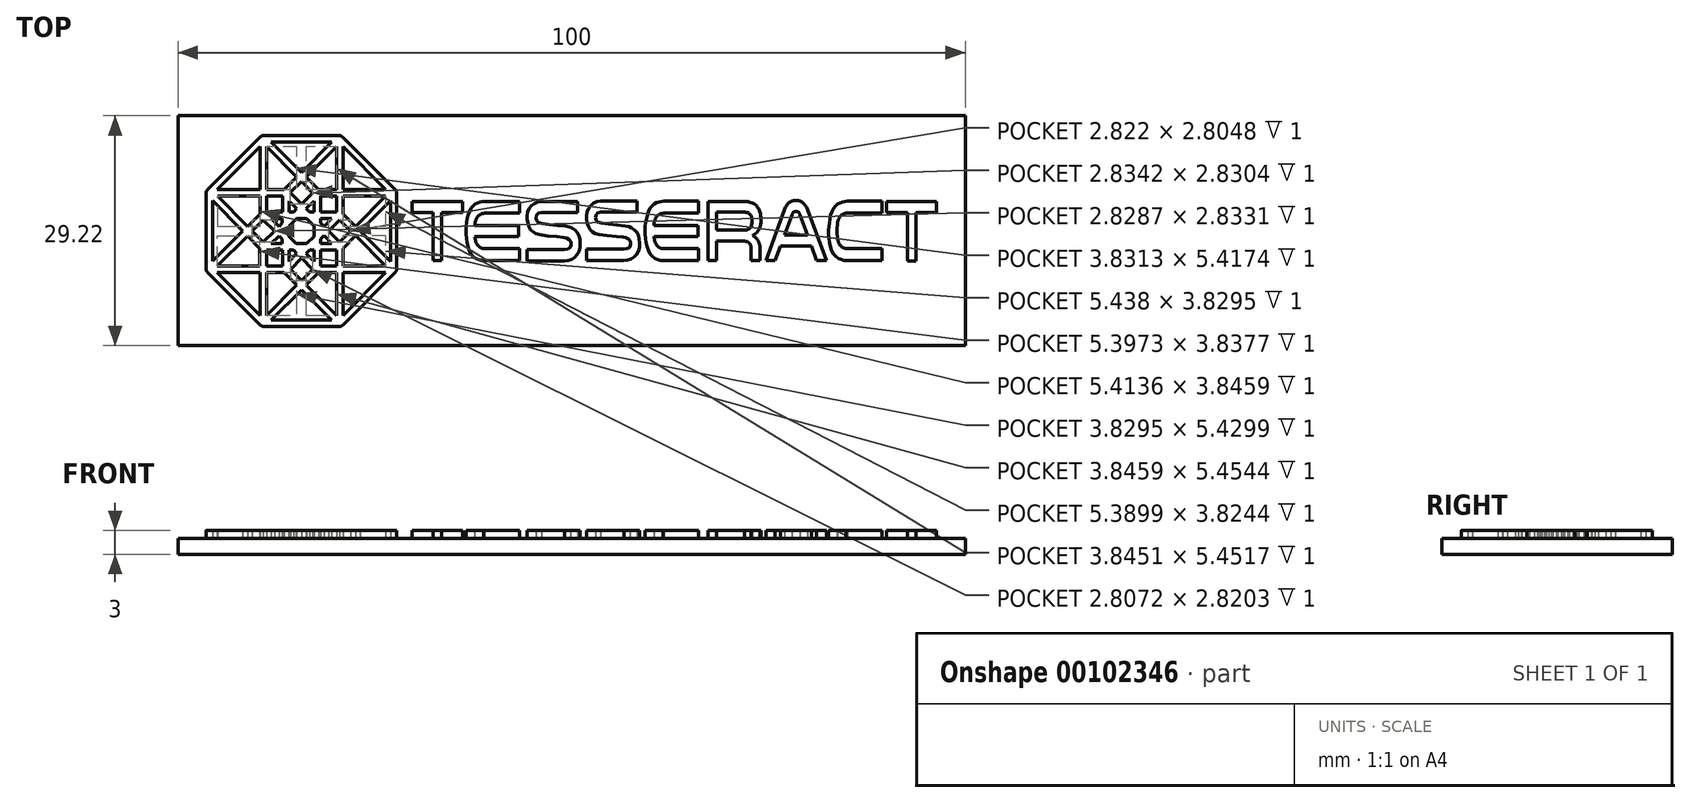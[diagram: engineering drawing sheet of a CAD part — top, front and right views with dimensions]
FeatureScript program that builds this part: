
annotation { "Feature Type Name" : "Feature", "Feature Type Description" : "" }
export const myFeature = defineFeature(function(context is Context, id is Id, definition is map)
    precondition{}
    {
        {
            var Q0;
            Q0=qCreatedBy(makeId("Top.planeOp"),FACE);
            var sketch = newSketch(context, id + "F0", { "sketchPlane" : qUnion([Q0])});
            skLineSegment(sketch, "E0.bottom", {"start": v(-42.05, 26.1) * mm, "end": v(57.95, 26.1) * mm});
            skLineSegment(sketch, "E0.top", {"start": v(-42.05, -3.12) * mm, "end": v(57.95, -3.12) * mm});
            skLineSegment(sketch, "E0.left", {"start": v(-42.05, 26.1) * mm, "end": v(-42.05, -3.12) * mm});
            skLineSegment(sketch, "E0.right", {"start": v(57.95, 26.1) * mm, "end": v(57.95, -3.12) * mm});
            skSolve(sketch);
        }
        {
            var Q0;
            Q0=makeQuery(id+"F0.imprint","IMPRINT",FACE,{"disambiguationData":[TD([[makeQuery(id+"F0.imprint","IMPRINT",EDGE,{"derivedFrom":sQuery(id+"F0.wireOp",EDGE,"E0.bottom")}),-1.0]])]});
            extrude(context, id + "F1", {"entities" : qUnion([Q0]), "oppositeDirection" : true, "depth" : 2 * mm});
        }
        {
            var Q0;
            Q0=makeQuery(id+"F1.opExtrude","CAP_FACE",FACE,{"disambiguationData":[OSD([sQuery(id+"F0.wireOp",EDGE,"E0.bottom"),sQuery(id+"F0.wireOp",EDGE,"E0.top"),sQuery(id+"F0.wireOp",EDGE,"E0.left"),sQuery(id+"F0.wireOp",EDGE,"E0.right")])],"isStart":true});
            var sketch = newSketch(context, id + "F2", { "sketchPlane" : qUnion([Q0])});
            skLineSegment(sketch, "E1.bottom", {"start": v(-12.32, 15.2) * mm, "end": v(-5.94, 15.2) * mm});
            skLineSegment(sketch, "E1.top", {"start": v(-12.32, 13.79) * mm, "end": v(-9.67, 13.79) * mm});
            skLineSegment(sketch, "E1.left", {"start": v(-12.32, 15.2) * mm, "end": v(-12.32, 13.79) * mm});
            skLineSegment(sketch, "E1.right", {"start": v(-5.94, 15.2) * mm, "end": v(-5.94, 13.79) * mm});
            skLineSegment(sketch, "E2.bottom", {"start": v(-9.67, 7.67) * mm, "end": v(-8.58, 7.67) * mm});
            skLineSegment(sketch, "E2.left", {"start": v(-9.67, 7.67) * mm, "end": v(-9.67, 13.79) * mm});
            skLineSegment(sketch, "E2.right", {"start": v(-8.58, 7.67) * mm, "end": v(-8.58, 13.79) * mm});
            skLineSegment(sketch, "E3.trimOffspring", {"start": v(-8.58, 13.79) * mm, "end": v(-5.94, 13.79) * mm});
            skLineSegment(sketch, "E4.bottom", {"start": v(1.34, 13.7) * mm, "end": v(-3.1, 13.7) * mm});
            skLineSegment(sketch, "E4.top", {"start": v(1.34, 15.22) * mm, "end": v(-3.1, 15.22) * mm});
            skLineSegment(sketch, "E4.left", {"start": v(1.34, 13.7) * mm, "end": v(1.34, 15.22) * mm});
            skLineSegment(sketch, "E5.bottom", {"start": v(1.23, 12.16) * mm, "end": v(-4.36, 12.16) * mm});
            skLineSegment(sketch, "E5.top", {"start": v(1.23, 10.75) * mm, "end": v(-4.36, 10.75) * mm});
            skLineSegment(sketch, "E5.left", {"start": v(1.23, 12.16) * mm, "end": v(1.23, 10.75) * mm});
            skLineSegment(sketch, "E6.bottom", {"start": v(1.32, 9.22) * mm, "end": v(-3.23, 9.22) * mm});
            skLineSegment(sketch, "E6.top", {"start": v(1.32, 7.67) * mm, "end": v(-3.23, 7.67) * mm});
            skLineSegment(sketch, "E6.left", {"start": v(1.32, 9.22) * mm, "end": v(1.32, 7.67) * mm});
            skFitSpline(sketch, "E7", {"points": [v(-3.23, 9.22) * mm, v(-3.64, 9.32) * mm, v(-4.1, 9.77) * mm, v(-4.36, 10.75) * mm, v(-4.36, 12.16) * mm, v(-4.2, 12.95) * mm, v(-3.83, 13.45) * mm, v(-3.1, 13.7) * mm], "startDerivative": vector(-3.91, 0.56) * mm, "endDerivative": vector(8.28, 0.62) * mm});
            skFitSpline(sketch, "E8", {"points": [v(-3.23, 7.67) * mm, v(-3.9, 7.8) * mm, v(-4.7, 8.36) * mm, v(-5.31, 9.73) * mm, v(-5.48, 11.49) * mm, v(-5.35, 12.85) * mm, v(-4.89, 14.25) * mm, v(-4.33, 14.85) * mm, v(-3.68, 15.16) * mm, v(-3.1, 15.22) * mm], "startDerivative": vector(-7.35, 0.76) * mm, "endDerivative": vector(6.93, 0.14) * mm});
            skLineSegment(sketch, "E9.bottom", {"start": v(8.7, 13.79) * mm, "end": v(4.1, 13.79) * mm});
            skLineSegment(sketch, "E9.top", {"start": v(8.7, 15.22) * mm, "end": v(4.1, 15.22) * mm});
            skLineSegment(sketch, "E9.left", {"start": v(8.7, 13.79) * mm, "end": v(8.7, 15.22) * mm});
            skLineSegment(sketch, "E10.bottom", {"start": v(2.27, 7.65) * mm, "end": v(7.07, 7.65) * mm});
            skLineSegment(sketch, "E10.top", {"start": v(2.27, 9.08) * mm, "end": v(7.07, 9.08) * mm});
            skLineSegment(sketch, "E10.left", {"start": v(2.27, 7.65) * mm, "end": v(2.27, 9.08) * mm});
            skFitSpline(sketch, "E11", {"points": [v(7.07, 9.08) * mm, v(7.53, 9.18) * mm, v(7.81, 9.41) * mm, v(7.87, 9.86) * mm, v(7.75, 10.29) * mm, v(7.27, 10.57) * mm, v(6.93, 10.63) * mm, v(3.75, 11) * mm, v(3.25, 11.18) * mm, v(2.8, 11.54) * mm, v(2.49, 12.03) * mm, v(2.32, 12.78) * mm, v(2.3, 13.41) * mm, v(2.47, 14.12) * mm, v(2.86, 14.68) * mm, v(3.43, 15.05) * mm, v(4.1, 15.22) * mm], "startDerivative": vector(9.28, 1.26) * mm, "endDerivative": vector(10.61, 2.02) * mm});
            skFitSpline(sketch, "E12", {"points": [v(7.07, 7.65) * mm, v(7.67, 7.76) * mm, v(8.33, 8.09) * mm, v(8.79, 8.66) * mm, v(9, 9.43) * mm, v(8.98, 10.38) * mm, v(8.85, 10.93) * mm, v(8.44, 11.5) * mm, v(7.9, 11.87) * mm, v(7.39, 12.03) * mm, v(4.2, 12.4) * mm, v(3.62, 12.63) * mm, v(3.45, 12.93) * mm, v(3.44, 13.32) * mm, v(3.63, 13.65) * mm, v(4.1, 13.79) * mm], "startDerivative": vector(9.62, 1.1) * mm, "endDerivative": vector(9.31, 1.4) * mm});
            skLineSegment(sketch, "E13.bottom", {"start": v(16.24, 13.83) * mm, "end": v(11.64, 13.83) * mm});
            skLineSegment(sketch, "E13.top", {"start": v(16.24, 15.26) * mm, "end": v(11.64, 15.26) * mm});
            skLineSegment(sketch, "E13.left", {"start": v(16.24, 13.83) * mm, "end": v(16.24, 15.26) * mm});
            skLineSegment(sketch, "E14.bottom", {"start": v(9.82, 7.7) * mm, "end": v(14.62, 7.7) * mm});
            skLineSegment(sketch, "E14.top", {"start": v(9.82, 9.13) * mm, "end": v(14.62, 9.13) * mm});
            skLineSegment(sketch, "E14.left", {"start": v(9.82, 7.7) * mm, "end": v(9.82, 9.13) * mm});
            skFitSpline(sketch, "E15", {"points": [v(14.62, 9.13) * mm, v(15.08, 9.23) * mm, v(15.36, 9.46) * mm, v(15.43, 9.9) * mm, v(15.3, 10.33) * mm, v(14.82, 10.61) * mm, v(14.48, 10.68) * mm, v(11.3, 11.04) * mm, v(10.8, 11.22) * mm, v(10.34, 11.58) * mm, v(10.04, 12.07) * mm, v(9.87, 12.83) * mm, v(9.85, 13.46) * mm, v(10.02, 14.17) * mm, v(10.4, 14.72) * mm, v(10.98, 15.1) * mm, v(11.64, 15.26) * mm], "startDerivative": vector(9.28, 1.26) * mm, "endDerivative": vector(10.61, 2.02) * mm});
            skFitSpline(sketch, "E16", {"points": [v(14.62, 7.7) * mm, v(15.22, 7.8) * mm, v(15.88, 8.14) * mm, v(16.34, 8.7) * mm, v(16.55, 9.48) * mm, v(16.53, 10.43) * mm, v(16.4, 10.97) * mm, v(15.99, 11.54) * mm, v(15.45, 11.91) * mm, v(14.94, 12.07) * mm, v(11.75, 12.45) * mm, v(11.17, 12.67) * mm, v(11, 12.98) * mm, v(11, 13.37) * mm, v(11.18, 13.7) * mm, v(11.64, 13.83) * mm], "startDerivative": vector(9.62, 1.1) * mm, "endDerivative": vector(9.31, 1.4) * mm});
            skLineSegment(sketch, "E17.bottom", {"start": v(24.09, 13.7) * mm, "end": v(19.65, 13.7) * mm});
            skLineSegment(sketch, "E17.top", {"start": v(24.09, 15.22) * mm, "end": v(19.65, 15.22) * mm});
            skLineSegment(sketch, "E17.left", {"start": v(24.09, 13.7) * mm, "end": v(24.09, 15.22) * mm});
            skLineSegment(sketch, "E18.bottom", {"start": v(23.98, 12.17) * mm, "end": v(18.4, 12.17) * mm});
            skLineSegment(sketch, "E18.top", {"start": v(23.98, 10.76) * mm, "end": v(18.4, 10.76) * mm});
            skLineSegment(sketch, "E18.left", {"start": v(23.98, 12.17) * mm, "end": v(23.98, 10.76) * mm});
            skLineSegment(sketch, "E19.bottom", {"start": v(24.07, 9.2) * mm, "end": v(19.53, 9.2) * mm});
            skLineSegment(sketch, "E19.top", {"start": v(24.07, 7.68) * mm, "end": v(19.53, 7.68) * mm});
            skLineSegment(sketch, "E19.left", {"start": v(24.07, 9.2) * mm, "end": v(24.07, 7.68) * mm});
            skFitSpline(sketch, "E20", {"points": [v(19.53, 9.2) * mm, v(19.12, 9.33) * mm, v(18.66, 9.78) * mm, v(18.4, 10.76) * mm, v(18.4, 12.17) * mm, v(18.56, 12.95) * mm, v(18.92, 13.45) * mm, v(19.65, 13.7) * mm], "startDerivative": vector(-3.91, 0.56) * mm, "endDerivative": vector(8.28, 0.62) * mm});
            skFitSpline(sketch, "E21", {"points": [v(19.53, 7.68) * mm, v(18.86, 7.8) * mm, v(18.05, 8.37) * mm, v(17.44, 9.73) * mm, v(17.28, 11.5) * mm, v(17.4, 12.85) * mm, v(17.86, 14.25) * mm, v(18.42, 14.85) * mm, v(19.08, 15.16) * mm, v(19.65, 15.22) * mm], "startDerivative": vector(-7.35, 0.76) * mm, "endDerivative": vector(6.93, 0.14) * mm});
            skLineSegment(sketch, "E22.bottom", {"start": v(47.93, 15.2) * mm, "end": v(54.31, 15.2) * mm});
            skLineSegment(sketch, "E22.top", {"start": v(47.93, 13.78) * mm, "end": v(50.58, 13.78) * mm});
            skLineSegment(sketch, "E22.left", {"start": v(47.93, 15.2) * mm, "end": v(47.93, 13.78) * mm});
            skLineSegment(sketch, "E22.right", {"start": v(54.31, 15.2) * mm, "end": v(54.31, 13.78) * mm});
            skLineSegment(sketch, "E23.bottom", {"start": v(50.58, 7.66) * mm, "end": v(51.67, 7.66) * mm});
            skLineSegment(sketch, "E23.left", {"start": v(50.58, 7.66) * mm, "end": v(50.58, 13.78) * mm});
            skLineSegment(sketch, "E23.right", {"start": v(51.67, 7.66) * mm, "end": v(51.67, 13.78) * mm});
            skLineSegment(sketch, "E24.trimOffspring", {"start": v(51.67, 13.78) * mm, "end": v(54.31, 13.78) * mm});
            skLineSegment(sketch, "E25.bottom", {"start": v(25.25, 7.67) * mm, "end": v(26.37, 7.67) * mm});
            skLineSegment(sketch, "E25.top", {"start": v(25.25, 15.22) * mm, "end": v(26.37, 15.22) * mm});
            skLineSegment(sketch, "E25.left", {"start": v(25.25, 7.67) * mm, "end": v(25.25, 15.22) * mm});
            skLineSegment(sketch, "E25.right", {"start": v(26.37, 7.67) * mm, "end": v(26.37, 10.15) * mm});
            skLineSegment(sketch, "E26.bottom", {"start": v(26.37, 11.57) * mm, "end": v(29.9, 11.57) * mm});
            skLineSegment(sketch, "E26.top", {"start": v(26.37, 10.15) * mm, "end": v(29.9, 10.15) * mm});
            skLineSegment(sketch, "E27.bottom", {"start": v(26.37, 15.22) * mm, "end": v(29.95, 15.22) * mm});
            skLineSegment(sketch, "E27.top", {"start": v(26.37, 13.83) * mm, "end": v(29.95, 13.83) * mm});
            skLineSegment(sketch, "E28.trimOffspring", {"start": v(26.37, 11.57) * mm, "end": v(26.37, 13.83) * mm});
            skFitSpline(sketch, "E29", {"points": [v(29.95, 13.83) * mm, v(30.39, 13.74) * mm, v(30.69, 13.42) * mm, v(30.87, 12.72) * mm, v(30.71, 12) * mm, v(30.37, 11.65) * mm, v(29.9, 11.57) * mm], "startDerivative": vector(3.1, -0.3) * mm, "endDerivative": vector(-3.16, -0.18) * mm});
            skFitSpline(sketch, "E30", {"points": [v(30.93, 10.88) * mm, v(31.31, 11.1) * mm, v(31.7, 11.56) * mm, v(31.94, 12.2) * mm, v(32, 12.98) * mm, v(31.9, 13.75) * mm, v(31.62, 14.38) * mm, v(31.1, 14.9) * mm, v(30.56, 15.13) * mm, v(30.3, 15.2) * mm, v(29.95, 15.22) * mm], "startDerivative": vector(4.45, 2.16) * mm, "endDerivative": vector(-4.85, 0.22) * mm});
            skLineSegment(sketch, "E31.bottom", {"start": v(30.73, 7.68) * mm, "end": v(31.87, 7.68) * mm});
            skLineSegment(sketch, "E31.left", {"start": v(30.73, 7.68) * mm, "end": v(30.73, 9.36) * mm});
            skLineSegment(sketch, "E31.right", {"start": v(31.87, 7.68) * mm, "end": v(31.87, 9.36) * mm});
            skFitSpline(sketch, "E32", {"points": [v(29.9, 10.15) * mm, v(30.22, 10.1) * mm, v(30.45, 9.96) * mm, v(30.63, 9.74) * mm, v(30.7, 9.55) * mm, v(30.73, 9.36) * mm], "startDerivative": vector(1.5, -0.05) * mm, "endDerivative": vector(0.26, -0.85) * mm});
            skFitSpline(sketch, "E33", {"points": [v(30.93, 10.88) * mm, v(31.14, 10.77) * mm, v(31.37, 10.57) * mm, v(31.63, 10.22) * mm, v(31.77, 9.87) * mm, v(31.84, 9.64) * mm, v(31.87, 9.47) * mm, v(31.87, 9.36) * mm], "startDerivative": vector(1.44, -0.68) * mm, "endDerivative": vector(0.02, -1.5) * mm});
            skLineSegment(sketch, "E34", {"start": v(32.62, 7.67) * mm, "end": v(33.8, 7.67) * mm});
            skLineSegment(sketch, "E35", {"start": v(33.8, 7.67) * mm, "end": v(34.48, 9.55) * mm});
            skLineSegment(sketch, "E36", {"start": v(34.48, 9.55) * mm, "end": v(38.4, 9.55) * mm});
            skLineSegment(sketch, "E37", {"start": v(38.4, 9.55) * mm, "end": v(39.06, 7.67) * mm});
            skLineSegment(sketch, "E38", {"start": v(39.06, 7.67) * mm, "end": v(40.3, 7.67) * mm});
            skLineSegment(sketch, "E39", {"start": v(40.3, 7.67) * mm, "end": v(37.91, 14.2) * mm});
            skLineSegment(sketch, "E40", {"start": v(34.97, 14.2) * mm, "end": v(32.62, 7.67) * mm});
            skLineSegment(sketch, "E41", {"start": v(34.98, 10.95) * mm, "end": v(37.88, 10.95) * mm});
            skLineSegment(sketch, "E42", {"start": v(37.88, 10.95) * mm, "end": v(36.95, 13.5) * mm});
            skLineSegment(sketch, "E43", {"start": v(35.9, 13.5) * mm, "end": v(34.98, 10.95) * mm});
            skFitSpline(sketch, "E44", {"points": [v(35.9, 13.5) * mm, v(36.06, 13.77) * mm, v(36.26, 13.91) * mm, v(36.43, 13.94) * mm, v(36.66, 13.9) * mm, v(36.84, 13.7) * mm, v(36.95, 13.5) * mm], "startDerivative": vector(0.68, 1.52) * mm, "endDerivative": vector(0.61, -1.19) * mm});
            skFitSpline(sketch, "E45", {"points": [v(34.97, 14.2) * mm, v(35.24, 14.68) * mm, v(35.63, 15.1) * mm, v(35.99, 15.27) * mm, v(36.83, 15.28) * mm, v(37.3, 15.06) * mm, v(37.66, 14.65) * mm, v(37.91, 14.2) * mm], "startDerivative": vector(1.68, 3.45) * mm, "endDerivative": vector(1.65, -3.33) * mm});
            skLineSegment(sketch, "E46.bottom", {"start": v(47.38, 13.72) * mm, "end": v(42.95, 13.72) * mm});
            skLineSegment(sketch, "E46.top", {"start": v(47.38, 15.23) * mm, "end": v(42.97, 15.23) * mm});
            skLineSegment(sketch, "E46.left", {"start": v(47.38, 13.72) * mm, "end": v(47.38, 15.23) * mm});
            skLineSegment(sketch, "E47.bottom", {"start": v(47.36, 9.21) * mm, "end": v(42.82, 9.21) * mm});
            skLineSegment(sketch, "E47.top", {"start": v(47.36, 7.68) * mm, "end": v(42.81, 7.68) * mm});
            skLineSegment(sketch, "E47.left", {"start": v(47.36, 9.21) * mm, "end": v(47.36, 7.68) * mm});
            skFitSpline(sketch, "E48", {"points": [v(42.82, 9.21) * mm, v(42.41, 9.34) * mm, v(41.95, 9.79) * mm, v(41.69, 10.77) * mm, v(41.69, 12.18) * mm, v(41.85, 12.96) * mm, v(42.22, 13.46) * mm, v(42.95, 13.72) * mm], "startDerivative": vector(-3.91, 0.56) * mm, "endDerivative": vector(8.28, 0.62) * mm});
            skFitSpline(sketch, "E49", {"points": [v(42.81, 7.68) * mm, v(42.21, 7.8) * mm, v(41.36, 8.3) * mm, v(40.75, 9.67) * mm, v(40.59, 11.43) * mm, v(40.71, 12.79) * mm, v(41.13, 14.2) * mm, v(41.72, 14.84) * mm, v(42.35, 15.13) * mm, v(42.97, 15.23) * mm], "startDerivative": vector(-7.35, 0.76) * mm, "endDerivative": vector(6.93, 0.14) * mm});
            skFitSpline(sketch, "E50", {"points": [v(41.69, 10.77) * mm, v(41.67, 11.4) * mm, v(41.69, 12.18) * mm], "startDerivative": vector(-0.09, 1.41) * mm, "endDerivative": vector(0.09, 1.4) * mm});
            skLineSegment(sketch, "E51", {"start": v(-27.98, 10.78) * mm, "end": v(-27.04, 9.85) * mm});
            skLineSegment(sketch, "E52", {"start": v(-27.04, 9.85) * mm, "end": v(-25.74, 9.85) * mm});
            skLineSegment(sketch, "E53", {"start": v(-25.74, 9.85) * mm, "end": v(-24.79, 10.77) * mm});
            skLineSegment(sketch, "E54", {"start": v(-24.79, 10.77) * mm, "end": v(-24.79, 12.1) * mm});
            skLineSegment(sketch, "E55", {"start": v(-24.79, 12.1) * mm, "end": v(-25.7, 13.04) * mm});
            skLineSegment(sketch, "E56", {"start": v(-25.7, 13.04) * mm, "end": v(-27.01, 13.04) * mm});
            skLineSegment(sketch, "E57", {"start": v(-27.01, 13.04) * mm, "end": v(-27.97, 12.1) * mm});
            skLineSegment(sketch, "E58", {"start": v(-27.97, 12.1) * mm, "end": v(-27.98, 10.78) * mm});
            skLineSegment(sketch, "E59", {"start": v(-23.95, 12.44) * mm, "end": v(-23.95, 13.04) * mm});
            skLineSegment(sketch, "E60", {"start": v(-23.95, 13.04) * mm, "end": v(-22.55, 13.04) * mm});
            skLineSegment(sketch, "E61", {"start": v(-22.55, 13.04) * mm, "end": v(-23.53, 12.03) * mm});
            skLineSegment(sketch, "E62", {"start": v(-23.53, 12.03) * mm, "end": v(-23.95, 12.44) * mm});
            skLineSegment(sketch, "E63", {"start": v(-23.96, 10.44) * mm, "end": v(-23.96, 9.84) * mm});
            skLineSegment(sketch, "E64", {"start": v(-23.96, 9.84) * mm, "end": v(-22.55, 9.84) * mm});
            skLineSegment(sketch, "E65", {"start": v(-22.55, 9.84) * mm, "end": v(-23.53, 10.85) * mm});
            skLineSegment(sketch, "E66", {"start": v(-23.53, 10.85) * mm, "end": v(-23.96, 10.44) * mm});
            skLineSegment(sketch, "E67", {"start": v(-22.94, 11.46) * mm, "end": v(-21.52, 10.03) * mm});
            skLineSegment(sketch, "E68", {"start": v(-21.52, 10.03) * mm, "end": v(-20.12, 11.42) * mm});
            skLineSegment(sketch, "E69", {"start": v(-20.12, 11.42) * mm, "end": v(-21.52, 12.83) * mm});
            skLineSegment(sketch, "E70", {"start": v(-21.52, 12.83) * mm, "end": v(-22.94, 11.46) * mm});
            skLineSegment(sketch, "E71", {"start": v(-27.97, 13.86) * mm, "end": v(-27.38, 13.86) * mm});
            skLineSegment(sketch, "E72", {"start": v(-27.38, 13.86) * mm, "end": v(-26.97, 14.28) * mm});
            skLineSegment(sketch, "E73", {"start": v(-26.97, 14.28) * mm, "end": v(-27.98, 15.26) * mm});
            skLineSegment(sketch, "E74", {"start": v(-27.98, 15.26) * mm, "end": v(-27.97, 13.86) * mm});
            skLineSegment(sketch, "E75", {"start": v(-25.37, 13.86) * mm, "end": v(-24.78, 13.86) * mm});
            skLineSegment(sketch, "E76", {"start": v(-24.78, 13.86) * mm, "end": v(-24.78, 15.28) * mm});
            skLineSegment(sketch, "E77", {"start": v(-24.78, 15.28) * mm, "end": v(-25.78, 14.28) * mm});
            skLineSegment(sketch, "E78", {"start": v(-25.78, 14.28) * mm, "end": v(-25.37, 13.86) * mm});
            skLineSegment(sketch, "E79", {"start": v(-27.8, 16.3) * mm, "end": v(-26.38, 14.88) * mm});
            skLineSegment(sketch, "E80", {"start": v(-26.38, 14.88) * mm, "end": v(-24.97, 16.29) * mm});
            skLineSegment(sketch, "E81", {"start": v(-24.97, 16.29) * mm, "end": v(-26.38, 17.7) * mm});
            skLineSegment(sketch, "E82", {"start": v(-26.38, 17.7) * mm, "end": v(-27.8, 16.3) * mm});
            skLineSegment(sketch, "E83", {"start": v(-30.22, 9.84) * mm, "end": v(-28.8, 9.84) * mm});
            skLineSegment(sketch, "E84", {"start": v(-28.8, 9.84) * mm, "end": v(-28.8, 10.43) * mm});
            skLineSegment(sketch, "E85", {"start": v(-28.8, 10.43) * mm, "end": v(-29.21, 10.83) * mm});
            skLineSegment(sketch, "E86", {"start": v(-29.21, 10.83) * mm, "end": v(-30.22, 9.84) * mm});
            skLineSegment(sketch, "E87", {"start": v(-30.2, 13.02) * mm, "end": v(-28.82, 13.02) * mm});
            skLineSegment(sketch, "E88", {"start": v(-28.82, 13.02) * mm, "end": v(-28.82, 12.43) * mm});
            skLineSegment(sketch, "E89", {"start": v(-28.82, 12.43) * mm, "end": v(-29.2, 12.04) * mm});
            skLineSegment(sketch, "E90", {"start": v(-29.2, 12.04) * mm, "end": v(-30.2, 13.02) * mm});
            skLineSegment(sketch, "E91", {"start": v(-32.64, 11.44) * mm, "end": v(-31.23, 10.02) * mm});
            skLineSegment(sketch, "E92", {"start": v(-31.23, 10.02) * mm, "end": v(-29.8, 11.42) * mm});
            skLineSegment(sketch, "E93", {"start": v(-29.8, 11.42) * mm, "end": v(-31.22, 12.85) * mm});
            skLineSegment(sketch, "E94", {"start": v(-31.22, 12.85) * mm, "end": v(-32.64, 11.44) * mm});
            skLineSegment(sketch, "E95", {"start": v(-27.98, 7.58) * mm, "end": v(-27.98, 9.01) * mm});
            skLineSegment(sketch, "E96", {"start": v(-27.98, 9.01) * mm, "end": v(-27.38, 9.01) * mm});
            skLineSegment(sketch, "E97", {"start": v(-27.38, 9.01) * mm, "end": v(-26.98, 8.58) * mm});
            skLineSegment(sketch, "E98", {"start": v(-26.98, 8.58) * mm, "end": v(-27.98, 7.58) * mm});
            skLineSegment(sketch, "E99", {"start": v(-25.37, 9) * mm, "end": v(-24.8, 9) * mm});
            skLineSegment(sketch, "E100", {"start": v(-24.8, 9) * mm, "end": v(-24.8, 7.59) * mm});
            skLineSegment(sketch, "E101", {"start": v(-24.8, 7.59) * mm, "end": v(-25.79, 8.58) * mm});
            skLineSegment(sketch, "E102", {"start": v(-25.79, 8.58) * mm, "end": v(-25.37, 9) * mm});
            skLineSegment(sketch, "E103", {"start": v(-26.37, 8) * mm, "end": v(-24.96, 6.57) * mm});
            skLineSegment(sketch, "E104", {"start": v(-24.96, 6.57) * mm, "end": v(-26.37, 5.17) * mm});
            skLineSegment(sketch, "E105", {"start": v(-26.37, 5.17) * mm, "end": v(-27.77, 6.58) * mm});
            skLineSegment(sketch, "E106", {"start": v(-27.77, 6.58) * mm, "end": v(-26.37, 8) * mm});
            skLineSegment(sketch, "E107.bottom", {"start": v(-30.81, 9) * mm, "end": v(-28.8, 9) * mm});
            skLineSegment(sketch, "E107.top", {"start": v(-30.81, 6.98) * mm, "end": v(-28.8, 6.98) * mm});
            skLineSegment(sketch, "E107.left", {"start": v(-30.81, 9) * mm, "end": v(-30.81, 6.98) * mm});
            skLineSegment(sketch, "E107.right", {"start": v(-28.8, 9) * mm, "end": v(-28.8, 6.98) * mm});
            skLineSegment(sketch, "E108.bottom", {"start": v(-23.95, 9) * mm, "end": v(-21.93, 9) * mm});
            skLineSegment(sketch, "E108.top", {"start": v(-23.95, 6.99) * mm, "end": v(-21.93, 6.99) * mm});
            skLineSegment(sketch, "E108.left", {"start": v(-23.95, 9) * mm, "end": v(-23.95, 6.99) * mm});
            skLineSegment(sketch, "E108.right", {"start": v(-21.93, 9) * mm, "end": v(-21.93, 6.99) * mm});
            skLineSegment(sketch, "E109.bottom", {"start": v(-30.82, 15.87) * mm, "end": v(-28.8, 15.87) * mm});
            skLineSegment(sketch, "E109.top", {"start": v(-30.82, 13.84) * mm, "end": v(-28.8, 13.84) * mm});
            skLineSegment(sketch, "E109.left", {"start": v(-30.82, 15.87) * mm, "end": v(-30.82, 13.84) * mm});
            skLineSegment(sketch, "E109.right", {"start": v(-28.8, 15.87) * mm, "end": v(-28.8, 13.84) * mm});
            skLineSegment(sketch, "E110.bottom", {"start": v(-23.95, 15.87) * mm, "end": v(-21.93, 15.87) * mm});
            skLineSegment(sketch, "E110.top", {"start": v(-23.95, 13.85) * mm, "end": v(-21.93, 13.85) * mm});
            skLineSegment(sketch, "E110.left", {"start": v(-23.95, 15.87) * mm, "end": v(-23.95, 13.85) * mm});
            skLineSegment(sketch, "E110.right", {"start": v(-21.93, 15.87) * mm, "end": v(-21.93, 13.85) * mm});
            skLineSegment(sketch, "E111", {"start": v(-37.09, 16.7) * mm, "end": v(-31.64, 16.7) * mm});
            skLineSegment(sketch, "E112", {"start": v(-31.64, 16.7) * mm, "end": v(-31.64, 22.15) * mm});
            skLineSegment(sketch, "E113", {"start": v(-31.64, 22.15) * mm, "end": v(-37.09, 16.7) * mm});
            skLineSegment(sketch, "E114", {"start": v(-30.82, 22.15) * mm, "end": v(-30.82, 16.73) * mm});
            skLineSegment(sketch, "E115", {"start": v(-30.82, 16.73) * mm, "end": v(-28.58, 16.73) * mm});
            skLineSegment(sketch, "E116", {"start": v(-28.58, 16.73) * mm, "end": v(-26.99, 18.31) * mm});
            skLineSegment(sketch, "E117", {"start": v(-26.99, 18.31) * mm, "end": v(-30.82, 22.15) * mm});
            skLineSegment(sketch, "E118", {"start": v(-30.21, 22.76) * mm, "end": v(-22.55, 22.76) * mm});
            skLineSegment(sketch, "E119", {"start": v(-22.55, 22.76) * mm, "end": v(-26.38, 18.9) * mm});
            skLineSegment(sketch, "E120", {"start": v(-26.38, 18.9) * mm, "end": v(-30.21, 22.76) * mm});
            skLineSegment(sketch, "E121", {"start": v(-21.93, 22.15) * mm, "end": v(-21.93, 16.7) * mm});
            skLineSegment(sketch, "E122", {"start": v(-21.93, 16.7) * mm, "end": v(-24.19, 16.7) * mm});
            skLineSegment(sketch, "E123", {"start": v(-24.19, 16.7) * mm, "end": v(-25.78, 18.3) * mm});
            skLineSegment(sketch, "E124", {"start": v(-25.78, 18.3) * mm, "end": v(-21.93, 22.15) * mm});
            skLineSegment(sketch, "E125", {"start": v(-21.1, 22.15) * mm, "end": v(-21.1, 16.71) * mm});
            skLineSegment(sketch, "E126", {"start": v(-21.1, 16.71) * mm, "end": v(-15.68, 16.71) * mm});
            skLineSegment(sketch, "E127", {"start": v(-15.68, 16.71) * mm, "end": v(-21.1, 22.15) * mm});
            skLineSegment(sketch, "E128", {"start": v(-21.1, 13.62) * mm, "end": v(-21.1, 15.86) * mm});
            skLineSegment(sketch, "E129", {"start": v(-21.1, 15.86) * mm, "end": v(-15.72, 15.86) * mm});
            skLineSegment(sketch, "E130", {"start": v(-15.72, 15.86) * mm, "end": v(-19.52, 12.04) * mm});
            skLineSegment(sketch, "E131", {"start": v(-19.52, 12.04) * mm, "end": v(-21.1, 13.62) * mm});
            skLineSegment(sketch, "E132", {"start": v(-15.07, 15.3) * mm, "end": v(-15.07, 7.57) * mm});
            skLineSegment(sketch, "E133", {"start": v(-15.07, 7.57) * mm, "end": v(-18.92, 11.44) * mm});
            skLineSegment(sketch, "E134", {"start": v(-18.92, 11.44) * mm, "end": v(-15.07, 15.3) * mm});
            skLineSegment(sketch, "E135", {"start": v(-21.1, 9.24) * mm, "end": v(-21.1, 7.02) * mm});
            skLineSegment(sketch, "E136", {"start": v(-21.1, 7.02) * mm, "end": v(-15.67, 7.02) * mm});
            skLineSegment(sketch, "E137", {"start": v(-15.67, 7.02) * mm, "end": v(-19.52, 10.84) * mm});
            skLineSegment(sketch, "E138", {"start": v(-19.52, 10.84) * mm, "end": v(-21.1, 9.24) * mm});
            skLineSegment(sketch, "E139", {"start": v(-21.1, 0.72) * mm, "end": v(-21.1, 6.16) * mm});
            skLineSegment(sketch, "E140", {"start": v(-21.1, 6.16) * mm, "end": v(-15.7, 6.16) * mm});
            skLineSegment(sketch, "E141", {"start": v(-15.7, 6.16) * mm, "end": v(-21.1, 0.72) * mm});
            skLineSegment(sketch, "E142", {"start": v(-24.2, 6.16) * mm, "end": v(-21.93, 6.16) * mm});
            skLineSegment(sketch, "E143", {"start": v(-21.93, 6.16) * mm, "end": v(-21.93, 0.7) * mm});
            skLineSegment(sketch, "E144", {"start": v(-21.93, 0.7) * mm, "end": v(-25.78, 4.57) * mm});
            skLineSegment(sketch, "E145", {"start": v(-25.78, 4.57) * mm, "end": v(-24.2, 6.16) * mm});
            skLineSegment(sketch, "E146", {"start": v(-30.21, 0.14) * mm, "end": v(-22.54, 0.14) * mm});
            skLineSegment(sketch, "E147", {"start": v(-22.54, 0.14) * mm, "end": v(-26.38, 3.97) * mm});
            skLineSegment(sketch, "E148", {"start": v(-26.38, 3.97) * mm, "end": v(-30.21, 0.14) * mm});
            skLineSegment(sketch, "E149", {"start": v(-30.8, 0.73) * mm, "end": v(-30.8, 6.16) * mm});
            skLineSegment(sketch, "E150", {"start": v(-30.8, 6.16) * mm, "end": v(-28.56, 6.16) * mm});
            skLineSegment(sketch, "E151", {"start": v(-28.56, 6.16) * mm, "end": v(-26.98, 4.57) * mm});
            skLineSegment(sketch, "E152", {"start": v(-26.98, 4.57) * mm, "end": v(-30.8, 0.73) * mm});
            skLineSegment(sketch, "E153", {"start": v(-31.65, 0.72) * mm, "end": v(-31.65, 6.16) * mm});
            skLineSegment(sketch, "E154", {"start": v(-31.65, 6.16) * mm, "end": v(-37.08, 6.16) * mm});
            skLineSegment(sketch, "E155", {"start": v(-37.08, 6.16) * mm, "end": v(-31.65, 0.72) * mm});
            skLineSegment(sketch, "E156", {"start": v(-37.06, 7) * mm, "end": v(-31.67, 7) * mm});
            skLineSegment(sketch, "E157", {"start": v(-31.67, 7) * mm, "end": v(-31.67, 9.24) * mm});
            skLineSegment(sketch, "E158", {"start": v(-31.67, 9.24) * mm, "end": v(-33.23, 10.84) * mm});
            skLineSegment(sketch, "E159", {"start": v(-33.23, 10.84) * mm, "end": v(-37.06, 7) * mm});
            skLineSegment(sketch, "E160", {"start": v(-37.67, 7.6) * mm, "end": v(-37.67, 15.29) * mm});
            skLineSegment(sketch, "E161", {"start": v(-37.67, 15.29) * mm, "end": v(-33.85, 11.44) * mm});
            skLineSegment(sketch, "E162", {"start": v(-33.85, 11.44) * mm, "end": v(-37.67, 7.6) * mm});
            skLineSegment(sketch, "E163", {"start": v(-37.06, 15.87) * mm, "end": v(-31.64, 15.87) * mm});
            skLineSegment(sketch, "E164", {"start": v(-31.64, 15.87) * mm, "end": v(-31.64, 13.62) * mm});
            skLineSegment(sketch, "E165", {"start": v(-31.64, 13.62) * mm, "end": v(-33.24, 12.03) * mm});
            skLineSegment(sketch, "E166", {"start": v(-37.06, 15.87) * mm, "end": v(-33.24, 12.03) * mm});
            skLineSegment(sketch, "E167", {"start": v(-38.5, 6.39) * mm, "end": v(-38.5, 16.5) * mm});
            skLineSegment(sketch, "E168", {"start": v(-31.42, -0.69) * mm, "end": v(-21.32, -0.69) * mm});
            skLineSegment(sketch, "E169", {"start": v(-14.26, 6.4) * mm, "end": v(-14.26, 16.5) * mm});
            skLineSegment(sketch, "E170", {"start": v(-21.38, 23.58) * mm, "end": v(-31.42, 23.58) * mm});
            skLineSegment(sketch, "E171", {"start": v(-38.5, 16.5) * mm, "end": v(-31.42, 23.58) * mm});
            skLineSegment(sketch, "E172", {"start": v(-21.38, 23.58) * mm, "end": v(-14.26, 16.5) * mm});
            skLineSegment(sketch, "E173", {"start": v(-21.32, -0.69) * mm, "end": v(-14.26, 6.4) * mm});
            skLineSegment(sketch, "E174", {"start": v(-38.5, 6.39) * mm, "end": v(-31.42, -0.69) * mm});
            skSolve(sketch);
        }
        {
            var Q0;
            Q0 = qSketchRegion(id + "F2", true);
            extrude(context, id + "F3", {"entities" : qUnion([Q0]), "operationType" : NewBodyOperationType.ADD, "depth" : 1 * mm});
        }
        {
            var Q0;
            Q0=makeQuery(id+"F3.opExtrude","SWEPT_EDGE",EDGE,{"disambiguationData":[OSD([sQuery(id+"F2.wireOp",EDGE,"E169"),sQuery(id+"F2.wireOp",EDGE,"E172")])]});
            var Q1;
            Q1=makeQuery(id+"F3.opExtrude","SWEPT_EDGE",EDGE,{"disambiguationData":[OSD([sQuery(id+"F2.wireOp",EDGE,"E169"),sQuery(id+"F2.wireOp",EDGE,"E173")])]});
            var Q2;
            Q2=makeQuery(id+"F3.opExtrude","SWEPT_EDGE",EDGE,{"disambiguationData":[OSD([sQuery(id+"F2.wireOp",EDGE,"E168"),sQuery(id+"F2.wireOp",EDGE,"E173")])]});
            var Q3;
            Q3=makeQuery(id+"F3.opExtrude","SWEPT_EDGE",EDGE,{"disambiguationData":[OSD([sQuery(id+"F2.wireOp",EDGE,"E168"),sQuery(id+"F2.wireOp",EDGE,"E174")])]});
            var Q4;
            Q4=makeQuery(id+"F3.opExtrude","SWEPT_EDGE",EDGE,{"disambiguationData":[OSD([sQuery(id+"F2.wireOp",EDGE,"E167"),sQuery(id+"F2.wireOp",EDGE,"E174")])]});
            var Q5;
            Q5=makeQuery(id+"F3.opExtrude","SWEPT_EDGE",EDGE,{"disambiguationData":[OSD([sQuery(id+"F2.wireOp",EDGE,"E170"),sQuery(id+"F2.wireOp",EDGE,"E172")])]});
            var Q6;
            Q6=makeQuery(id+"F3.opExtrude","SWEPT_EDGE",EDGE,{"disambiguationData":[OSD([sQuery(id+"F2.wireOp",EDGE,"E170"),sQuery(id+"F2.wireOp",EDGE,"E171")])]});
            var Q7;
            Q7=makeQuery(id+"F3.opExtrude","SWEPT_EDGE",EDGE,{"disambiguationData":[OSD([sQuery(id+"F2.wireOp",EDGE,"E167"),sQuery(id+"F2.wireOp",EDGE,"E171")])]});
            fillet(context, id + "F4", {"entities" : qUnion([Q0, Q1, Q2, Q3, Q4, Q5, Q6, Q7]), "radius" : 0.7 * mm, "tangentPropagation" : true, "allowEdgeOverflow" : false});
        }
    });
